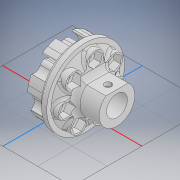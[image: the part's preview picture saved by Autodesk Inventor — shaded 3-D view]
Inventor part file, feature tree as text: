
AUTODESK INVENTOR PART (.ipt)
format: ipt  version: 2022 (Build 260153000, 153)  size: 965,632 bytes
history: native  units: mm
features: extrude x7, sketch x7, other x6, fillet x2, pattern_circular x1, projected_geometry x1, reference x1
ambient origin geometry x8: Origin, YZ Plane, XZ Plane, XY Plane, X Axis, Y Axis, Z Axis, Center Point
bodies: Body1 (feature_tree)
feature tree (25):
  extrude  "Выдавливание1"  Depth=14.0mm TaperAngle=0.0deg
  extrude  "Выдавливание2"  Depth=6.5mm
  fillet  "Сопряжение1"  Radius=7.3mm
  pattern_circular  "Круговой массив1"  [2 undecoded]
  extrude  "Выдавливание3"  Depth=1.75mm
  extrude  "Выдавливание4"  Depth=70.0mm TaperAngle=360.0deg
  extrude  "Выдавливание5"  Depth=10.0mm TaperAngle=0.0deg
  other  "РабПлоскость1"
  extrude  "Выдавливание6"  Depth=12.0mm
  extrude  "Выдавливание7"  Depth=10.0mm TaperAngle=0.0deg
  fillet  "Сопряжение2"  Radius=10.0mm
  other  "Твердое тело5"
  sketch  "Эскиз1"
  sketch  "Эскиз2"
  sketch  "Эскиз3"
  sketch  "Эскиз4"
  sketch  "Эскиз5"
  projected_geometry  "Спроецированная петля1"
  sketch  "Эскиз6"
  reference  "Ссылка1"
  sketch  "Эскиз7"
  other  "Solid1:4"
  other  "<path> - Крепеж мотора СБ.iam"
  other  "000.002 - Крепеж мотора СБ.iam"
  other  "000.002.003 - Металлическая вставка:1"
note: 2 required parameter values undecoded (feature->parameter linkage not recoverable at this tier; creation-order binding heuristic only, values carry confidence <= 0.55)
note: 1 file-system path scrubbed to <path> (originals preserved in map.json)
